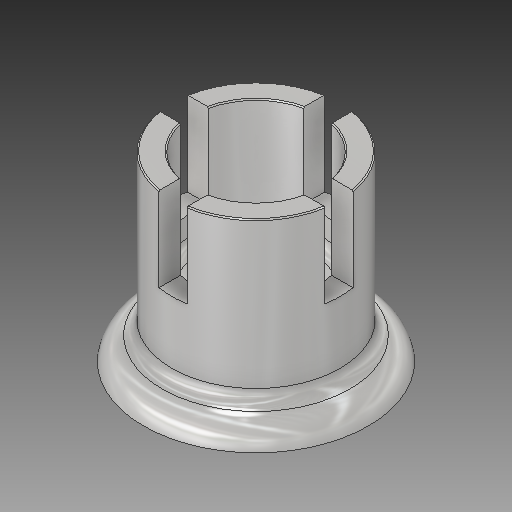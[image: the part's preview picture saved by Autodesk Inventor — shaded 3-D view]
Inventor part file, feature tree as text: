
AUTODESK INVENTOR PART (.ipt)
format: ipt  version: 2020 (Build 240168000, 168)  size: 230,400 bytes
history: native  units: in
note: dims shown in document units (in); Inventor stores cm internally (conversion verified against a paired STEP export)
features: sketch x2, revolve x1, chamfer x1, extrude x1, pattern_circular x1
ambient origin geometry x8: Origin, YZ Plane, XZ Plane, XY Plane, X Axis, Y Axis, Z Axis, Center Point
bodies: Solid1 (feature_tree)
feature tree (6):
  revolve  "Revolution1"  [1 undecoded]
  chamfer  "Chamfer1"  Distance=0.5in
  extrude  "Extrusion1"  Depth=0.125in
  pattern_circular  "Circular Pattern1"  [2 undecoded]
  sketch  "Sketch1"  dims[d0=0.8125in d1=0.75in]
  sketch  "Sketch2"  dims[d2=0.5625in d3=0.5in d4=0.125in d5=1.0in d6=0.0625in d7=0.125in d8=0.15in d9=90.0deg d10=0.0625in d11=0.005in d12=0.125in d13=45.0deg d14=0.125in d15=0.0625in d16=0.375in d17=0.0in d18=1.5748in d19=360.0deg]
note: 3 required parameter values undecoded (feature->parameter linkage not recoverable at this tier; creation-order binding heuristic only, values carry confidence <= 0.55)